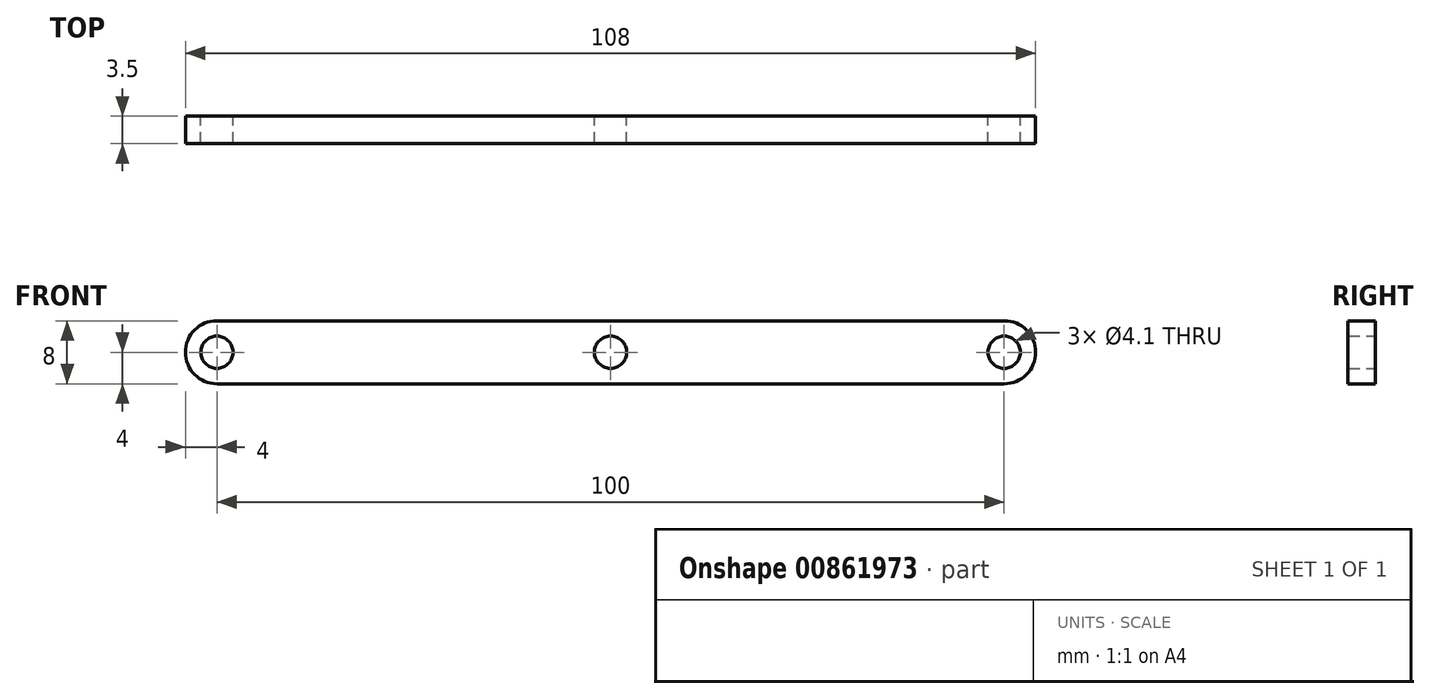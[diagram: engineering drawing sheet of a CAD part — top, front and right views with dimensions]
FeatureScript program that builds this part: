
annotation { "Feature Type Name" : "Feature", "Feature Type Description" : "" }
export const myFeature = defineFeature(function(context is Context, id is Id, definition is map)
    precondition{}
    {
        {
            var Q0;
            Q0=qCreatedBy(makeId("Front.planeOp"),FACE);
            var sketch = newSketch(context, id + "F0", { "sketchPlane" : qUnion([Q0])});
            skArc(sketch, "E0", {"start": v(2.5, 8) * mm, "mid": v(-1.5, 4) * mm, "end": v(2.5, 0) * mm});
            skArc(sketch, "E1", {"start": v(102.5, 0) * mm, "mid": v(106.5, 4) * mm, "end": v(102.5, 8) * mm});
            skCircle(sketch, "E2", {"center": v(102.5, 4) * mm, "radius": 2.05 * mm});
            skCircle(sketch, "E3", {"center": v(2.5, 4) * mm, "radius": 2.05 * mm});
            skLineSegment(sketch, "E4", {"start": v(102.5, 8) * mm, "end": v(2.5, 8) * mm});
            skLineSegment(sketch, "E5", {"start": v(2.5, 0) * mm, "end": v(102.5, 0) * mm});
            skCircle(sketch, "E6", {"center": v(52.5, 4) * mm, "radius": 2.05 * mm});
            skPoint(sketch, "E7.orphan", {"position": v(52.5, 8) * mm});
            skPoint(sketch, "E8.end.orphan", {"position": v(52.5, 0) * mm});
            skSolve(sketch);
        }
        {
            var Q0;
            Q0=qSketchRegion(id+"F0",true);
            extrude(context, id + "F1", {"entities" : qUnion([Q0]), "depth" : 3.5 * mm, "offsetDistance" : 25 * mm, "symmetric" : true});
        }
    });
